# Revit family: WSW390
name_source: partatom
category: Plumbing Fixtures
units: mm (PartAtom-declared; Revit-internal decimal feet)

## family parameters
Cut with Voids When Loaded = No
Host = Face
Maintain Annotation Orientation = No
OmniClass Number = 23.45.05.14.14
OmniClass Title = Sinks/Lavatories
Part Type = Normal
Room Calculation Point = No
Round Connector Dimension = Use Diameter
Shared = Yes

## types (1)
- WSW390-TC1
    ADA Compliant = Yes
    Assembly Code = D2010440
    Body Material = Metal-Acorn-304-Stainless_Steel-16-Gauge
    Bowl Shape = Trough
    CW Connection = Yes
    CWFU = 3
    Cold Water Connection Diameter = 1 5/16"
    Cold Water Connection Radius = 21/32"
    DSW000-TC1Accessory: Single 24" Wide Trap Enclosure = Yes
    Default Elevation = 34"
    Description = Neo-Metro® by Acorn® provides this durable, stainless steel trough sink. It is available in sizes to accommodate from one to four users. The design is perfect for high-traffic restrooms, incorporating ample personal space while reducing wet, slippery floors.

The WSW000 Series hand washing station is wall mounted and features a unique “wedge”-shaped trough (patent pending) with a polished stainless steel finish and rounded corners.

Optional trap enclosures are available to conceal hot and cold mixing valves and supply/waste connections while providing easy maintenance access. The enclosure is fabricated of 16 gauge, type 304 stainless steel with a satin finish. It is available in 24" (610 mm) or 54" (1,372 mm) widths.

When mounted at 34" (864 mm) from the finished floor, the fixture will comply with ANSI, UFAS, CBC, OBC, and ADA requirements. Compliance is subject to the interpretation and requirements of the local code authority.
    Diameter For Soap Knockout = 1 5/16"
    EG - Enviro-Glaze, Specify Color = No
    Flow Rate = 0.5 GPM (1.9 LPM) for faucet type
    HW Connection = Yes
    HWFU = 3
    Height = 19 3/4"
    Hot Water Connection Diameter = 1 5/16"
    Hot Water Connection Radius = 21/32"
    IAPMO Compliance = Fixture complies with ANSI, UFAS, CBC and ADA 2010 requirements for accessibility.
    Installation Type = Wall Mounted
    Length = 90"
    Manufacturer = Acorn Engineering
    Model = WSW390
    PS1000 - PS Pump Soap Dispenser, Specify number = No
    Price = Prices may vary. Please consult Manufacturer Representative for most up-to-date price list.
    Product Documentation Link = https://www.acorneng.com
    Product Page URL = https://www.acorneng.com
    SW000 - F50 H&C Wristblade Faucet, Gooseneck Spout = No
    SW000 - F51 H&C Wristblade Faucet, Spout = No
    SW000 - F60 S/T Sensor Operated Faucet,J Spout, Plate = Yes
    SW000 - F70 S/T Pushbutton Metering Faucet, Plate = No
    SW000 - PT Daisy Strainer, Tailpiece, 1-1/2” P-Trap, Plastic = No
    SW000 - PTC Daisy Strainer, Tailpiece, 1-1/2” P-Trap, Chrome = No
    Sink Inner Length = 87 7/8"
    Sink Inner Width = 15 3/4"
    Trap Enclosure Width = 24"
    Type Comments = WEDGE™ Stainless Steel Trough Sink
    URL = https://acorneng.com
    Vent Connection = No
    WFU = 4
    Waste Connection = Yes
    Waste Connection Diameter = 1 1/2"
    Waste Connection Radius = 3/4"
    Width = 21 5/8"

## geometry (parser evidence)
native form markers: Sweep x2
no freeform markers — native parametric forms only
